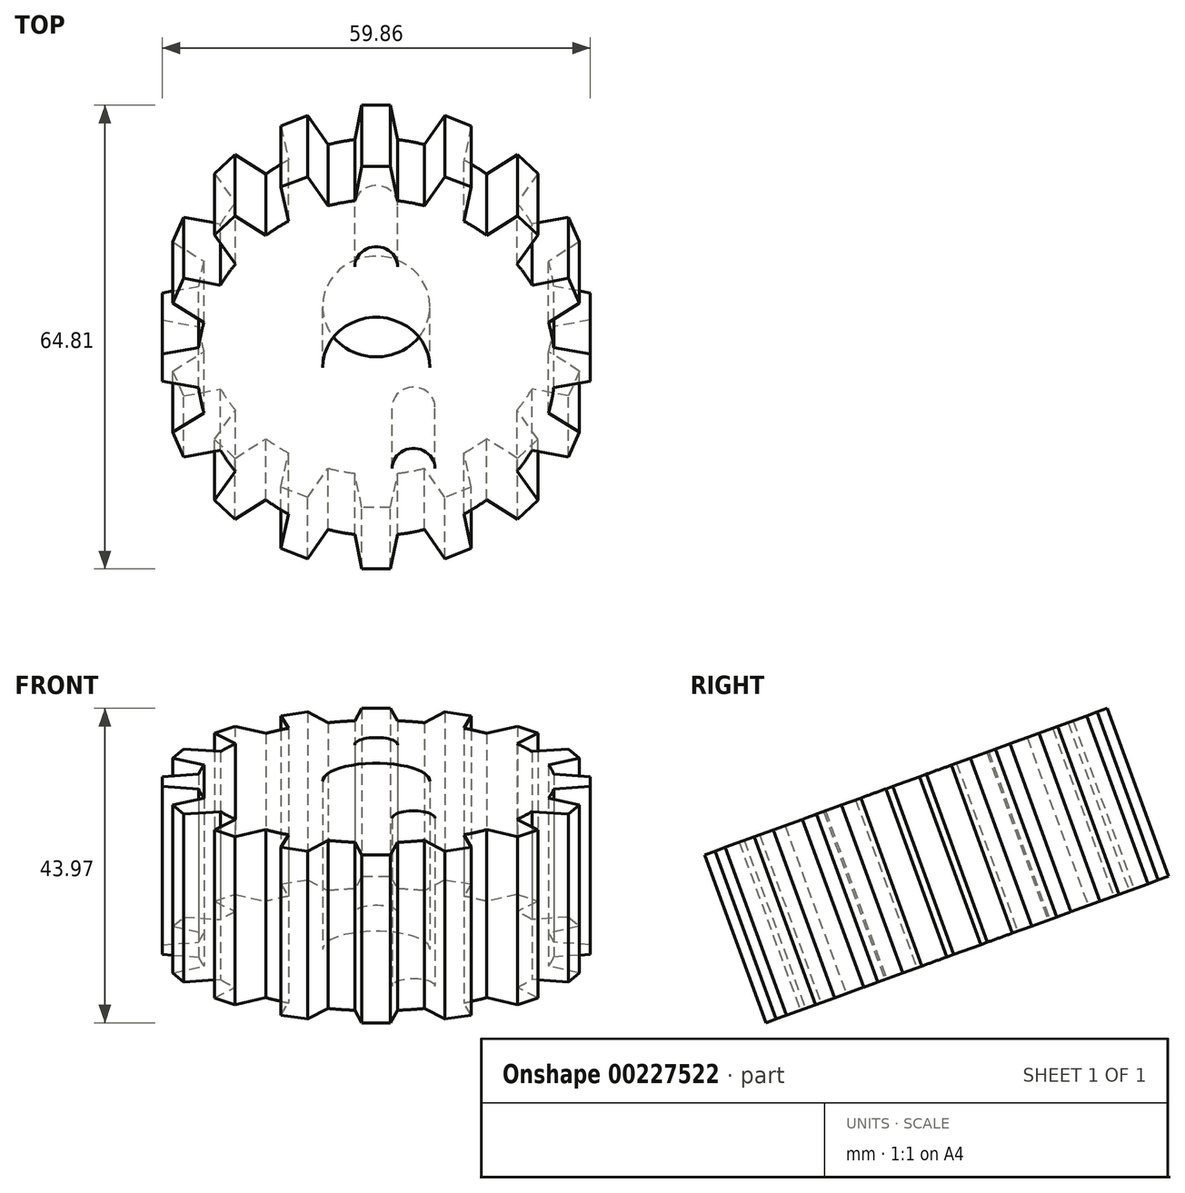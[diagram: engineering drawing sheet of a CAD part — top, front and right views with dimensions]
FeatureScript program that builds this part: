
annotation { "Feature Type Name" : "Feature", "Feature Type Description" : "" }
export const myFeature = defineFeature(function(context is Context, id is Id, definition is map)
    precondition{}
    {
        {
            var Q0;
            Q0=qCreatedBy(makeId("Top.planeOp"),FACE);
            var sketch = newSketch(context, id + "F0", { "sketchPlane" : qUnion([Q0])});
            skArc(sketch, "E0", {"start": v(2, 29.93) * mm, "mid": v(0, 30) * mm, "end": v(-2, 29.93) * mm});
            skCircle(sketch, "E1", {"center": v(0, 0) * mm, "radius": 7.5 * mm});
            skArc(sketch, "E2", {"start": v(-12.27, 21.78) * mm, "mid": v(-13.89, 20.79) * mm, "end": v(-15.43, 19.67) * mm});
            skCircle(sketch, "E3", {"center": v(0, 0) * mm, "radius": 15 * mm, "construction": true});
            skLineSegment(sketch, "E4", {"start": v(-2, 29.93) * mm, "end": v(-3, 24.82) * mm});
            skLineSegment(sketch, "E5", {"start": v(2, 29.93) * mm, "end": v(3, 24.82) * mm});
            skLineSegment(sketch, "E6", {"start": v(-2, 29.93) * mm, "end": v(2, 29.93) * mm});
            skLineSegment(sketch, "E7.1.0", {"start": v(9.6, 28.42) * mm, "end": v(6.73, 24.08) * mm});
            skLineSegment(sketch, "E7.1.1", {"start": v(9.6, 28.42) * mm, "end": v(13.3, 26.89) * mm});
            skLineSegment(sketch, "E7.1.2", {"start": v(13.3, 26.89) * mm, "end": v(12.27, 21.78) * mm});
            skLineSegment(sketch, "E7.2.0", {"start": v(19.75, 22.58) * mm, "end": v(15.43, 19.67) * mm});
            skLineSegment(sketch, "E7.2.1", {"start": v(19.75, 22.58) * mm, "end": v(22.58, 19.75) * mm});
            skLineSegment(sketch, "E7.2.2", {"start": v(22.58, 19.75) * mm, "end": v(19.67, 15.43) * mm});
            skLineSegment(sketch, "E7.3.0", {"start": v(26.89, 13.3) * mm, "end": v(21.78, 12.27) * mm});
            skLineSegment(sketch, "E7.3.1", {"start": v(26.89, 13.3) * mm, "end": v(28.42, 9.6) * mm});
            skLineSegment(sketch, "E7.3.2", {"start": v(28.42, 9.6) * mm, "end": v(24.08, 6.73) * mm});
            skLineSegment(sketch, "E7.4.0", {"start": v(29.93, 2) * mm, "end": v(24.82, 3) * mm});
            skLineSegment(sketch, "E7.4.1", {"start": v(29.93, 2) * mm, "end": v(29.93, -2) * mm});
            skLineSegment(sketch, "E7.4.2", {"start": v(29.93, -2) * mm, "end": v(24.82, -3) * mm});
            skLineSegment(sketch, "E7.5.0", {"start": v(28.42, -9.6) * mm, "end": v(24.08, -6.73) * mm});
            skLineSegment(sketch, "E7.5.1", {"start": v(28.42, -9.6) * mm, "end": v(26.89, -13.3) * mm});
            skLineSegment(sketch, "E7.5.2", {"start": v(26.89, -13.3) * mm, "end": v(21.78, -12.27) * mm});
            skLineSegment(sketch, "E7.6.0", {"start": v(22.58, -19.75) * mm, "end": v(19.67, -15.43) * mm});
            skLineSegment(sketch, "E7.6.1", {"start": v(22.58, -19.75) * mm, "end": v(19.75, -22.58) * mm});
            skLineSegment(sketch, "E7.6.2", {"start": v(19.75, -22.58) * mm, "end": v(15.43, -19.67) * mm});
            skLineSegment(sketch, "E7.7.0", {"start": v(13.3, -26.89) * mm, "end": v(12.27, -21.78) * mm});
            skLineSegment(sketch, "E7.7.1", {"start": v(13.3, -26.89) * mm, "end": v(9.6, -28.42) * mm});
            skLineSegment(sketch, "E7.7.2", {"start": v(9.6, -28.42) * mm, "end": v(6.73, -24.08) * mm});
            skLineSegment(sketch, "E7.8.0", {"start": v(2, -29.93) * mm, "end": v(3, -24.82) * mm});
            skLineSegment(sketch, "E7.8.1", {"start": v(2, -29.93) * mm, "end": v(-2, -29.93) * mm});
            skLineSegment(sketch, "E7.8.2", {"start": v(-2, -29.93) * mm, "end": v(-3, -24.82) * mm});
            skLineSegment(sketch, "E7.9.0", {"start": v(-9.6, -28.42) * mm, "end": v(-6.73, -24.08) * mm});
            skLineSegment(sketch, "E7.9.1", {"start": v(-9.6, -28.42) * mm, "end": v(-13.3, -26.89) * mm});
            skLineSegment(sketch, "E7.9.2", {"start": v(-13.3, -26.89) * mm, "end": v(-12.27, -21.78) * mm});
            skLineSegment(sketch, "E7.10.0", {"start": v(-19.75, -22.58) * mm, "end": v(-15.43, -19.67) * mm});
            skLineSegment(sketch, "E7.10.1", {"start": v(-19.75, -22.58) * mm, "end": v(-22.58, -19.75) * mm});
            skLineSegment(sketch, "E7.10.2", {"start": v(-22.58, -19.75) * mm, "end": v(-19.67, -15.43) * mm});
            skLineSegment(sketch, "E7.11.0", {"start": v(-26.89, -13.3) * mm, "end": v(-21.78, -12.27) * mm});
            skLineSegment(sketch, "E7.11.1", {"start": v(-26.89, -13.3) * mm, "end": v(-28.42, -9.6) * mm});
            skLineSegment(sketch, "E7.11.2", {"start": v(-28.42, -9.6) * mm, "end": v(-24.08, -6.73) * mm});
            skLineSegment(sketch, "E7.12.0", {"start": v(-29.93, -2) * mm, "end": v(-24.82, -3) * mm});
            skLineSegment(sketch, "E7.12.1", {"start": v(-29.93, -2) * mm, "end": v(-29.93, 2) * mm});
            skLineSegment(sketch, "E7.12.2", {"start": v(-29.93, 2) * mm, "end": v(-24.82, 3) * mm});
            skLineSegment(sketch, "E7.13.0", {"start": v(-28.42, 9.6) * mm, "end": v(-24.08, 6.73) * mm});
            skLineSegment(sketch, "E7.13.1", {"start": v(-28.42, 9.6) * mm, "end": v(-26.89, 13.3) * mm});
            skLineSegment(sketch, "E7.13.2", {"start": v(-26.89, 13.3) * mm, "end": v(-21.78, 12.27) * mm});
            skLineSegment(sketch, "E7.14.0", {"start": v(-22.58, 19.75) * mm, "end": v(-19.67, 15.43) * mm});
            skLineSegment(sketch, "E7.14.1", {"start": v(-22.58, 19.75) * mm, "end": v(-19.75, 22.58) * mm});
            skLineSegment(sketch, "E7.14.2", {"start": v(-19.75, 22.58) * mm, "end": v(-15.43, 19.67) * mm});
            skLineSegment(sketch, "E7.15.0", {"start": v(-13.3, 26.89) * mm, "end": v(-12.27, 21.78) * mm});
            skLineSegment(sketch, "E7.15.1", {"start": v(-13.3, 26.89) * mm, "end": v(-9.6, 28.42) * mm});
            skLineSegment(sketch, "E7.15.2", {"start": v(-9.6, 28.42) * mm, "end": v(-6.73, 24.08) * mm});
            skCircle(sketch, "E8", {"center": v(0, 15) * mm, "radius": 3 * mm});
            skPoint(sketch, "E9.1.0", {"position": v(5.21, 0) * mm});
            skCircle(sketch, "E9.1.1", {"center": v(5.21, -15) * mm, "radius": 3 * mm});
            skPoint(sketch, "E9.3.0", {"position": v(5.21, 0) * mm});
            skCircle(sketch, "E9.3.1", {"center": v(5.21, -15) * mm, "radius": 3 * mm});
            skPoint(sketch, "E9.center", {"position": v(2.6, 0) * mm});
            skArc(sketch, "E10.trimOffspring", {"start": v(-3, 24.82) * mm, "mid": v(-4.88, 24.52) * mm, "end": v(-6.73, 24.08) * mm});
            skArc(sketch, "E11.trimOffspring", {"start": v(6.73, 24.08) * mm, "mid": v(4.88, 24.52) * mm, "end": v(3, 24.82) * mm});
            skArc(sketch, "E12.trimOffspring", {"start": v(15.43, 19.67) * mm, "mid": v(13.89, 20.79) * mm, "end": v(12.27, 21.78) * mm});
            skArc(sketch, "E13.trimOffspring", {"start": v(21.78, 12.27) * mm, "mid": v(20.79, 13.89) * mm, "end": v(19.67, 15.43) * mm});
            skArc(sketch, "E14.trimOffspring", {"start": v(24.82, 3) * mm, "mid": v(24.52, 4.88) * mm, "end": v(24.08, 6.73) * mm});
            skArc(sketch, "E15.trimOffspring", {"start": v(24.08, -6.73) * mm, "mid": v(24.52, -4.88) * mm, "end": v(24.82, -3) * mm});
            skArc(sketch, "E16.trimOffspring", {"start": v(19.67, -15.43) * mm, "mid": v(20.79, -13.89) * mm, "end": v(21.78, -12.27) * mm});
            skArc(sketch, "E17.trimOffspring", {"start": v(12.27, -21.78) * mm, "mid": v(13.89, -20.79) * mm, "end": v(15.43, -19.67) * mm});
            skArc(sketch, "E18.trimOffspring", {"start": v(3, -24.82) * mm, "mid": v(4.88, -24.52) * mm, "end": v(6.73, -24.08) * mm});
            skArc(sketch, "E19.trimOffspring", {"start": v(-6.73, -24.08) * mm, "mid": v(-4.88, -24.52) * mm, "end": v(-3, -24.82) * mm});
            skArc(sketch, "E20.trimOffspring", {"start": v(-15.43, -19.67) * mm, "mid": v(-13.89, -20.79) * mm, "end": v(-12.27, -21.78) * mm});
            skArc(sketch, "E21.trimOffspring", {"start": v(-21.78, -12.27) * mm, "mid": v(-20.79, -13.89) * mm, "end": v(-19.67, -15.43) * mm});
            skArc(sketch, "E22.trimOffspring", {"start": v(-24.82, -3) * mm, "mid": v(-24.52, -4.88) * mm, "end": v(-24.08, -6.73) * mm});
            skArc(sketch, "E23.trimOffspring", {"start": v(-24.08, 6.73) * mm, "mid": v(-24.52, 4.88) * mm, "end": v(-24.82, 3) * mm});
            skArc(sketch, "E24.trimOffspring", {"start": v(-19.67, 15.43) * mm, "mid": v(-20.79, 13.89) * mm, "end": v(-21.78, 12.27) * mm});
            skSolve(sketch);
        }
        {
            var Q0;
            Q0=makeQuery(id+"F0.imprint","IMPRINT",FACE,{"disambiguationData":[TD([[makeQuery(id+"F0.imprint","IMPRINT",EDGE,{"derivedFrom":sQuery(id+"F0.wireOp",EDGE,"E1")}),-1.0]])]});
            extrude(context, id + "F1", {"entities" : qUnion([Q0]), "depth" : 25 * mm});
        }
        {
            var Q0;
            Q0=makeQuery(id+"F1.opExtrude","CAP_FACE",FACE,{"disambiguationData":[OSD([sQuery(id+"F0.wireOp",EDGE,"E1"),sQuery(id+"F0.wireOp",EDGE,"E2"),sQuery(id+"F0.wireOp",EDGE,"E4"),sQuery(id+"F0.wireOp",EDGE,"E5"),sQuery(id+"F0.wireOp",EDGE,"E6"),sQuery(id+"F0.wireOp",EDGE,"E7.1.0"),sQuery(id+"F0.wireOp",EDGE,"E7.1.1"),sQuery(id+"F0.wireOp",EDGE,"E7.1.2"),sQuery(id+"F0.wireOp",EDGE,"E7.2.0"),sQuery(id+"F0.wireOp",EDGE,"E7.2.1"),sQuery(id+"F0.wireOp",EDGE,"E7.2.2"),sQuery(id+"F0.wireOp",EDGE,"E7.3.0"),sQuery(id+"F0.wireOp",EDGE,"E7.3.1"),sQuery(id+"F0.wireOp",EDGE,"E7.3.2"),sQuery(id+"F0.wireOp",EDGE,"E7.4.0"),sQuery(id+"F0.wireOp",EDGE,"E7.4.1"),sQuery(id+"F0.wireOp",EDGE,"E7.4.2"),sQuery(id+"F0.wireOp",EDGE,"E7.5.0"),sQuery(id+"F0.wireOp",EDGE,"E7.5.1"),sQuery(id+"F0.wireOp",EDGE,"E7.5.2"),sQuery(id+"F0.wireOp",EDGE,"E7.6.0"),sQuery(id+"F0.wireOp",EDGE,"E7.6.1"),sQuery(id+"F0.wireOp",EDGE,"E7.6.2"),sQuery(id+"F0.wireOp",EDGE,"E7.7.0"),sQuery(id+"F0.wireOp",EDGE,"E7.7.1"),sQuery(id+"F0.wireOp",EDGE,"E7.7.2"),sQuery(id+"F0.wireOp",EDGE,"E7.8.0"),sQuery(id+"F0.wireOp",EDGE,"E7.8.1"),sQuery(id+"F0.wireOp",EDGE,"E7.8.2"),sQuery(id+"F0.wireOp",EDGE,"E7.9.0"),sQuery(id+"F0.wireOp",EDGE,"E7.9.1"),sQuery(id+"F0.wireOp",EDGE,"E7.9.2"),sQuery(id+"F0.wireOp",EDGE,"E7.10.0"),sQuery(id+"F0.wireOp",EDGE,"E7.10.1"),sQuery(id+"F0.wireOp",EDGE,"E7.10.2"),sQuery(id+"F0.wireOp",EDGE,"E7.11.0"),sQuery(id+"F0.wireOp",EDGE,"E7.11.1"),sQuery(id+"F0.wireOp",EDGE,"E7.11.2"),sQuery(id+"F0.wireOp",EDGE,"E7.12.0"),sQuery(id+"F0.wireOp",EDGE,"E7.12.1"),sQuery(id+"F0.wireOp",EDGE,"E7.12.2"),sQuery(id+"F0.wireOp",EDGE,"E7.13.0"),sQuery(id+"F0.wireOp",EDGE,"E7.13.1"),sQuery(id+"F0.wireOp",EDGE,"E7.13.2"),sQuery(id+"F0.wireOp",EDGE,"E7.14.0"),sQuery(id+"F0.wireOp",EDGE,"E7.14.1"),sQuery(id+"F0.wireOp",EDGE,"E7.14.2"),sQuery(id+"F0.wireOp",EDGE,"E7.15.0"),sQuery(id+"F0.wireOp",EDGE,"E7.15.1"),sQuery(id+"F0.wireOp",EDGE,"E7.15.2"),sQuery(id+"F0.wireOp",EDGE,"E9.3.1"),sQuery(id+"F0.wireOp",EDGE,"E8"),sQuery(id+"F0.wireOp",EDGE,"E10.trimOffspring"),sQuery(id+"F0.wireOp",EDGE,"E11.trimOffspring"),sQuery(id+"F0.wireOp",EDGE,"E12.trimOffspring"),sQuery(id+"F0.wireOp",EDGE,"E13.trimOffspring"),sQuery(id+"F0.wireOp",EDGE,"E14.trimOffspring"),sQuery(id+"F0.wireOp",EDGE,"E15.trimOffspring"),sQuery(id+"F0.wireOp",EDGE,"E16.trimOffspring"),sQuery(id+"F0.wireOp",EDGE,"E17.trimOffspring"),sQuery(id+"F0.wireOp",EDGE,"E18.trimOffspring"),sQuery(id+"F0.wireOp",EDGE,"E19.trimOffspring"),sQuery(id+"F0.wireOp",EDGE,"E20.trimOffspring"),sQuery(id+"F0.wireOp",EDGE,"E21.trimOffspring"),sQuery(id+"F0.wireOp",EDGE,"E22.trimOffspring"),sQuery(id+"F0.wireOp",EDGE,"E23.trimOffspring"),sQuery(id+"F0.wireOp",EDGE,"E24.trimOffspring")])],"isStart":false});
            var sketch = newSketch(context, id + "F2", { "sketchPlane" : qUnion([Q0])});
            skLineSegment(sketch, "E25.0.0", {"start": v(2, 29.93) * mm, "end": v(-2, 29.93) * mm});
            skLineSegment(sketch, "E25.0.1", {"start": v(-2, 29.93) * mm, "end": v(-3, 24.82) * mm});
            skArc(sketch, "E25.0.2", {"start": v(-3, 24.82) * mm, "mid": v(-4.88, 24.52) * mm, "end": v(-6.73, 24.08) * mm});
            skLineSegment(sketch, "E25.0.3", {"start": v(-6.73, 24.08) * mm, "end": v(-9.6, 28.42) * mm});
            skLineSegment(sketch, "E25.0.4", {"start": v(-9.6, 28.42) * mm, "end": v(-13.3, 26.89) * mm});
            skLineSegment(sketch, "E25.0.5", {"start": v(-13.3, 26.89) * mm, "end": v(-12.27, 21.78) * mm});
            skArc(sketch, "E25.0.6", {"start": v(-12.27, 21.78) * mm, "mid": v(-13.89, 20.79) * mm, "end": v(-15.43, 19.67) * mm});
            skLineSegment(sketch, "E25.0.7", {"start": v(-15.43, 19.67) * mm, "end": v(-19.75, 22.58) * mm});
            skLineSegment(sketch, "E25.0.8", {"start": v(-19.75, 22.58) * mm, "end": v(-22.58, 19.75) * mm});
            skLineSegment(sketch, "E25.0.9", {"start": v(-22.58, 19.75) * mm, "end": v(-19.67, 15.43) * mm});
            skArc(sketch, "E25.0.10", {"start": v(-19.67, 15.43) * mm, "mid": v(-20.79, 13.89) * mm, "end": v(-21.78, 12.27) * mm});
            skLineSegment(sketch, "E25.0.11", {"start": v(-21.78, 12.27) * mm, "end": v(-26.89, 13.3) * mm});
            skLineSegment(sketch, "E25.0.12", {"start": v(-26.89, 13.3) * mm, "end": v(-28.42, 9.6) * mm});
            skLineSegment(sketch, "E25.0.13", {"start": v(-28.42, 9.6) * mm, "end": v(-24.08, 6.73) * mm});
            skArc(sketch, "E25.0.14", {"start": v(-24.08, 6.73) * mm, "mid": v(-24.52, 4.88) * mm, "end": v(-24.82, 3) * mm});
            skLineSegment(sketch, "E25.0.15", {"start": v(-24.82, 3) * mm, "end": v(-29.93, 2) * mm});
            skLineSegment(sketch, "E25.0.16", {"start": v(-29.93, 2) * mm, "end": v(-29.93, -2) * mm});
            skLineSegment(sketch, "E25.0.17", {"start": v(-29.93, -2) * mm, "end": v(-24.82, -3) * mm});
            skArc(sketch, "E25.0.18", {"start": v(-24.82, -3) * mm, "mid": v(-24.52, -4.88) * mm, "end": v(-24.08, -6.73) * mm});
            skLineSegment(sketch, "E25.0.19", {"start": v(-24.08, -6.73) * mm, "end": v(-28.42, -9.6) * mm});
            skLineSegment(sketch, "E25.0.20", {"start": v(-28.42, -9.6) * mm, "end": v(-26.89, -13.3) * mm});
            skLineSegment(sketch, "E25.0.21", {"start": v(-26.89, -13.3) * mm, "end": v(-21.78, -12.27) * mm});
            skArc(sketch, "E25.0.22", {"start": v(-21.78, -12.27) * mm, "mid": v(-20.79, -13.89) * mm, "end": v(-19.67, -15.43) * mm});
            skLineSegment(sketch, "E25.0.23", {"start": v(-19.67, -15.43) * mm, "end": v(-22.58, -19.75) * mm});
            skLineSegment(sketch, "E25.0.24", {"start": v(-22.58, -19.75) * mm, "end": v(-19.75, -22.58) * mm});
            skLineSegment(sketch, "E25.0.25", {"start": v(-19.75, -22.58) * mm, "end": v(-15.43, -19.67) * mm});
            skArc(sketch, "E25.0.26", {"start": v(-15.43, -19.67) * mm, "mid": v(-13.89, -20.79) * mm, "end": v(-12.27, -21.78) * mm});
            skLineSegment(sketch, "E25.0.27", {"start": v(-12.27, -21.78) * mm, "end": v(-13.3, -26.89) * mm});
            skLineSegment(sketch, "E25.0.28", {"start": v(-13.3, -26.89) * mm, "end": v(-9.6, -28.42) * mm});
            skLineSegment(sketch, "E25.0.29", {"start": v(-9.6, -28.42) * mm, "end": v(-6.73, -24.08) * mm});
            skArc(sketch, "E25.0.30", {"start": v(-6.73, -24.08) * mm, "mid": v(-4.88, -24.52) * mm, "end": v(-3, -24.82) * mm});
            skLineSegment(sketch, "E25.0.31", {"start": v(-3, -24.82) * mm, "end": v(-2, -29.93) * mm});
            skLineSegment(sketch, "E25.0.32", {"start": v(-2, -29.93) * mm, "end": v(2, -29.93) * mm});
            skLineSegment(sketch, "E25.0.33", {"start": v(2, -29.93) * mm, "end": v(3, -24.82) * mm});
            skArc(sketch, "E25.0.34", {"start": v(3, -24.82) * mm, "mid": v(4.88, -24.52) * mm, "end": v(6.73, -24.08) * mm});
            skLineSegment(sketch, "E25.0.35", {"start": v(6.73, -24.08) * mm, "end": v(9.6, -28.42) * mm});
            skLineSegment(sketch, "E25.0.36", {"start": v(9.6, -28.42) * mm, "end": v(13.3, -26.89) * mm});
            skLineSegment(sketch, "E25.0.37", {"start": v(13.3, -26.89) * mm, "end": v(12.27, -21.78) * mm});
            skArc(sketch, "E25.0.38", {"start": v(12.27, -21.78) * mm, "mid": v(13.89, -20.79) * mm, "end": v(15.43, -19.67) * mm});
            skLineSegment(sketch, "E25.0.39", {"start": v(15.43, -19.67) * mm, "end": v(19.75, -22.58) * mm});
            skLineSegment(sketch, "E25.0.40", {"start": v(19.75, -22.58) * mm, "end": v(22.58, -19.75) * mm});
            skLineSegment(sketch, "E25.0.41", {"start": v(22.58, -19.75) * mm, "end": v(19.67, -15.43) * mm});
            skArc(sketch, "E25.0.42", {"start": v(19.67, -15.43) * mm, "mid": v(20.79, -13.89) * mm, "end": v(21.78, -12.27) * mm});
            skLineSegment(sketch, "E25.0.43", {"start": v(21.78, -12.27) * mm, "end": v(26.89, -13.3) * mm});
            skLineSegment(sketch, "E25.0.44", {"start": v(26.89, -13.3) * mm, "end": v(28.42, -9.6) * mm});
            skLineSegment(sketch, "E25.0.45", {"start": v(28.42, -9.6) * mm, "end": v(24.08, -6.73) * mm});
            skArc(sketch, "E25.0.46", {"start": v(24.08, -6.73) * mm, "mid": v(24.52, -4.88) * mm, "end": v(24.82, -3) * mm});
            skLineSegment(sketch, "E25.0.47", {"start": v(24.82, -3) * mm, "end": v(29.93, -2) * mm});
            skLineSegment(sketch, "E25.0.48", {"start": v(29.93, -2) * mm, "end": v(29.93, 2) * mm});
            skLineSegment(sketch, "E25.0.49", {"start": v(29.93, 2) * mm, "end": v(24.82, 3) * mm});
            skArc(sketch, "E25.0.50", {"start": v(24.82, 3) * mm, "mid": v(24.52, 4.88) * mm, "end": v(24.08, 6.73) * mm});
            skLineSegment(sketch, "E25.0.51", {"start": v(24.08, 6.73) * mm, "end": v(28.42, 9.6) * mm});
            skLineSegment(sketch, "E25.0.52", {"start": v(28.42, 9.6) * mm, "end": v(26.89, 13.3) * mm});
            skLineSegment(sketch, "E25.0.53", {"start": v(26.89, 13.3) * mm, "end": v(21.78, 12.27) * mm});
            skArc(sketch, "E25.0.54", {"start": v(21.78, 12.27) * mm, "mid": v(20.79, 13.89) * mm, "end": v(19.67, 15.43) * mm});
            skLineSegment(sketch, "E25.0.55", {"start": v(19.67, 15.43) * mm, "end": v(22.58, 19.75) * mm});
            skLineSegment(sketch, "E25.0.56", {"start": v(22.58, 19.75) * mm, "end": v(19.75, 22.58) * mm});
            skLineSegment(sketch, "E25.0.57", {"start": v(19.75, 22.58) * mm, "end": v(15.43, 19.67) * mm});
            skArc(sketch, "E25.0.58", {"start": v(15.43, 19.67) * mm, "mid": v(13.89, 20.79) * mm, "end": v(12.27, 21.78) * mm});
            skLineSegment(sketch, "E25.0.59", {"start": v(12.27, 21.78) * mm, "end": v(13.3, 26.89) * mm});
            skLineSegment(sketch, "E25.0.60", {"start": v(13.3, 26.89) * mm, "end": v(9.6, 28.42) * mm});
            skLineSegment(sketch, "E25.0.61", {"start": v(9.6, 28.42) * mm, "end": v(6.73, 24.08) * mm});
            skArc(sketch, "E25.0.62", {"start": v(6.73, 24.08) * mm, "mid": v(4.88, 24.52) * mm, "end": v(3, 24.82) * mm});
            skLineSegment(sketch, "E25.0.63", {"start": v(3, 24.82) * mm, "end": v(2, 29.93) * mm});
            skLineSegment(sketch, "E26", {"start": v(-35.28, 0) * mm, "end": v(36.78, 0) * mm, "construction": true});
            skSolve(sketch);
        }
        {
            var Q0;
            Q0=makeQuery(id+"F1.opExtrude","SWEPT_BODY",BODY,{"disambiguationData":[OSD([sQuery(id+"F0.wireOp",EDGE,"E1"),sQuery(id+"F0.wireOp",EDGE,"E2"),sQuery(id+"F0.wireOp",EDGE,"E4"),sQuery(id+"F0.wireOp",EDGE,"E5"),sQuery(id+"F0.wireOp",EDGE,"E6"),sQuery(id+"F0.wireOp",EDGE,"E7.1.0"),sQuery(id+"F0.wireOp",EDGE,"E7.1.1"),sQuery(id+"F0.wireOp",EDGE,"E7.1.2"),sQuery(id+"F0.wireOp",EDGE,"E7.2.0"),sQuery(id+"F0.wireOp",EDGE,"E7.2.1"),sQuery(id+"F0.wireOp",EDGE,"E7.2.2"),sQuery(id+"F0.wireOp",EDGE,"E7.3.0"),sQuery(id+"F0.wireOp",EDGE,"E7.3.1"),sQuery(id+"F0.wireOp",EDGE,"E7.3.2"),sQuery(id+"F0.wireOp",EDGE,"E7.4.0"),sQuery(id+"F0.wireOp",EDGE,"E7.4.1"),sQuery(id+"F0.wireOp",EDGE,"E7.4.2"),sQuery(id+"F0.wireOp",EDGE,"E7.5.0"),sQuery(id+"F0.wireOp",EDGE,"E7.5.1"),sQuery(id+"F0.wireOp",EDGE,"E7.5.2"),sQuery(id+"F0.wireOp",EDGE,"E7.6.0"),sQuery(id+"F0.wireOp",EDGE,"E7.6.1"),sQuery(id+"F0.wireOp",EDGE,"E7.6.2"),sQuery(id+"F0.wireOp",EDGE,"E7.7.0"),sQuery(id+"F0.wireOp",EDGE,"E7.7.1"),sQuery(id+"F0.wireOp",EDGE,"E7.7.2"),sQuery(id+"F0.wireOp",EDGE,"E7.8.0"),sQuery(id+"F0.wireOp",EDGE,"E7.8.1"),sQuery(id+"F0.wireOp",EDGE,"E7.8.2"),sQuery(id+"F0.wireOp",EDGE,"E7.9.0"),sQuery(id+"F0.wireOp",EDGE,"E7.9.1"),sQuery(id+"F0.wireOp",EDGE,"E7.9.2"),sQuery(id+"F0.wireOp",EDGE,"E7.10.0"),sQuery(id+"F0.wireOp",EDGE,"E7.10.1"),sQuery(id+"F0.wireOp",EDGE,"E7.10.2"),sQuery(id+"F0.wireOp",EDGE,"E7.11.0"),sQuery(id+"F0.wireOp",EDGE,"E7.11.1"),sQuery(id+"F0.wireOp",EDGE,"E7.11.2"),sQuery(id+"F0.wireOp",EDGE,"E7.12.0"),sQuery(id+"F0.wireOp",EDGE,"E7.12.1"),sQuery(id+"F0.wireOp",EDGE,"E7.12.2"),sQuery(id+"F0.wireOp",EDGE,"E7.13.0"),sQuery(id+"F0.wireOp",EDGE,"E7.13.1"),sQuery(id+"F0.wireOp",EDGE,"E7.13.2"),sQuery(id+"F0.wireOp",EDGE,"E7.14.0"),sQuery(id+"F0.wireOp",EDGE,"E7.14.1"),sQuery(id+"F0.wireOp",EDGE,"E7.14.2"),sQuery(id+"F0.wireOp",EDGE,"E7.15.0"),sQuery(id+"F0.wireOp",EDGE,"E7.15.1"),sQuery(id+"F0.wireOp",EDGE,"E7.15.2"),sQuery(id+"F0.wireOp",EDGE,"E9.3.1"),sQuery(id+"F0.wireOp",EDGE,"E8"),sQuery(id+"F0.wireOp",EDGE,"E10.trimOffspring"),sQuery(id+"F0.wireOp",EDGE,"E11.trimOffspring"),sQuery(id+"F0.wireOp",EDGE,"E12.trimOffspring"),sQuery(id+"F0.wireOp",EDGE,"E13.trimOffspring"),sQuery(id+"F0.wireOp",EDGE,"E14.trimOffspring"),sQuery(id+"F0.wireOp",EDGE,"E15.trimOffspring"),sQuery(id+"F0.wireOp",EDGE,"E16.trimOffspring"),sQuery(id+"F0.wireOp",EDGE,"E17.trimOffspring"),sQuery(id+"F0.wireOp",EDGE,"E18.trimOffspring"),sQuery(id+"F0.wireOp",EDGE,"E19.trimOffspring"),sQuery(id+"F0.wireOp",EDGE,"E20.trimOffspring"),sQuery(id+"F0.wireOp",EDGE,"E21.trimOffspring"),sQuery(id+"F0.wireOp",EDGE,"E22.trimOffspring"),sQuery(id+"F0.wireOp",EDGE,"E23.trimOffspring"),sQuery(id+"F0.wireOp",EDGE,"E24.trimOffspring")])]});
            var Q1;
            Q1=sQuery(id+"F2.wireOp",EDGE,"E26");
            transform(context, id + "F3", {"entities" : qUnion([Q0]), "transformType" : TransformType.ROTATION, "transformAxis" : qUnion([Q1]), "angle" : 20 * degree, "makeCopy" : false});
        }
    });
